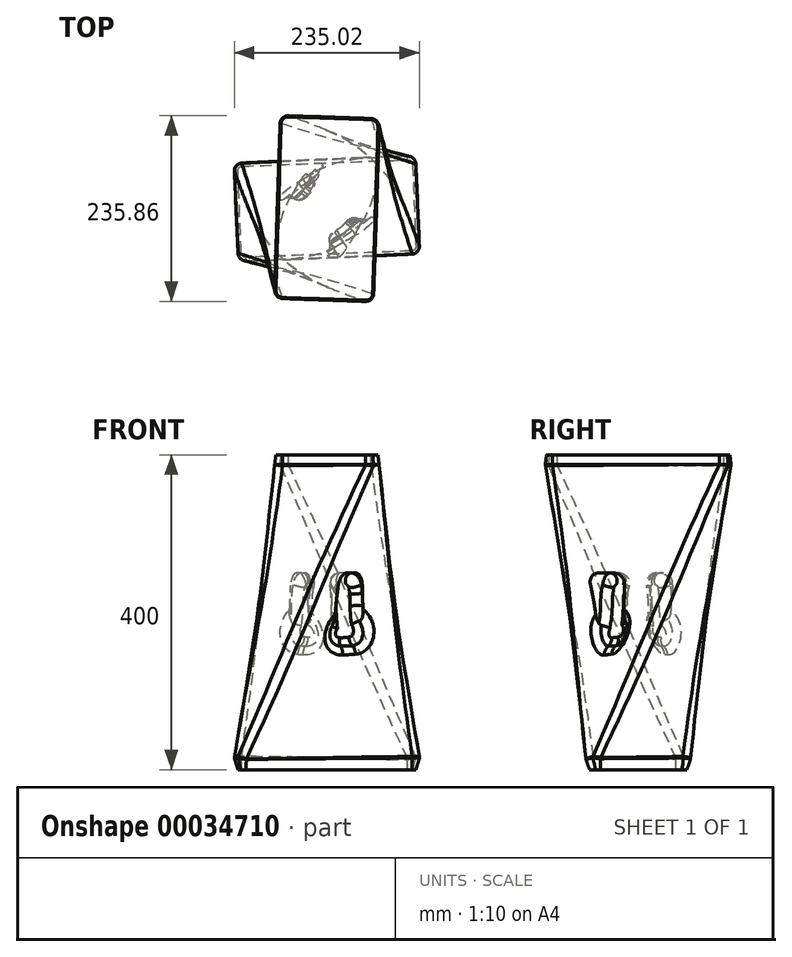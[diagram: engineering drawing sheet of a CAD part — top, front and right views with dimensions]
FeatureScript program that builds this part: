
annotation { "Feature Type Name" : "Feature", "Feature Type Description" : "" }
export const myFeature = defineFeature(function(context is Context, id is Id, definition is map)
    precondition{}
    {
        {
            var Q0;
            Q0=qCreatedBy(makeId("Top.planeOp"),FACE);
            var sketch = newSketch(context, id + "F0", { "sketchPlane" : qUnion([Q0])});
            skLineSegment(sketch, "E0.bottom", {"start": v(-120, 65) * mm, "end": v(120, 65) * mm});
            skLineSegment(sketch, "E0.top", {"start": v(-120, -65) * mm, "end": v(120, -65) * mm});
            skLineSegment(sketch, "E0.left", {"start": v(-120, 65) * mm, "end": v(-120, -65) * mm});
            skLineSegment(sketch, "E0.right", {"start": v(120, 65) * mm, "end": v(120, -65) * mm});
            skSolve(sketch);
        }
        {
            var Q0;
            Q0=qCreatedBy(makeId("Top.planeOp"),FACE);
            cPlane(context, id + "F1", {"entities" : qUnion([Q0]), "cplaneType" : CPlaneType.OFFSET, "offset" : 400 * mm, "width" : 150 * mm, "height" : 150 * mm});
        }
        {
            var Q0;
            Q0=qCreatedBy(id+"F1.planeOp",FACE);
            var sketch = newSketch(context, id + "F2", { "sketchPlane" : qUnion([Q0])});
            skLineSegment(sketch, "E1.bottom", {"start": v(-65, 120) * mm, "end": v(65, 120) * mm});
            skLineSegment(sketch, "E1.top", {"start": v(-65, -120) * mm, "end": v(65, -120) * mm});
            skLineSegment(sketch, "E1.left", {"start": v(-65, 120) * mm, "end": v(-65, -120) * mm});
            skLineSegment(sketch, "E1.right", {"start": v(65, 120) * mm, "end": v(65, -120) * mm});
            skSolve(sketch);
        }
        {
            var Q0;
            Q0=makeQuery(id+"F0.imprint","IMPRINT",FACE,{"disambiguationData":[TD([[makeQuery(id+"F0.imprint","IMPRINT",EDGE,{"derivedFrom":sQuery(id+"F0.wireOp",EDGE,"E0.bottom")}),-1.0]])]});
            var Q1;
            Q1=makeQuery(id+"F2.imprint","IMPRINT",FACE,{"disambiguationData":[TD([[makeQuery(id+"F2.imprint","IMPRINT",EDGE,{"derivedFrom":sQuery(id+"F2.wireOp",EDGE,"E1.bottom")}),-1.0]])]});
            var Q2;
            Q2=sQuery(id+"F0.wireOp",VERTEX,"E0.left.end");
            var Q3;
            Q3=sQuery(id+"F2.wireOp",VERTEX,"E1.top.end");
            loft(context, id + "F3", {"sheetProfilesArray" : [{ "sheetProfileEntities" : qUnion([Q0]) }, { "sheetProfileEntities" : qUnion([Q1]) }], "matchConnections" : true, "connections" : [{ "connectionEntities" : qUnion([Q2, Q3]), "connectionEdgeQueries" : qUnion([]), "connectionEdgeParameters" : [] }]});
        }
        {
            var Q0;
            Q0=makeQuery(id+"F3.opLoft","SWEPT_EDGE",EDGE,{"disambiguationData":[OSD([sQuery(id+"F0.wireOp",EDGE,"E0.top"),sQuery(id+"F0.wireOp",EDGE,"E0.left"),sQuery(id+"F2.wireOp",EDGE,"E1.top"),sQuery(id+"F2.wireOp",EDGE,"E1.right")])]});
            var Q1;
            Q1=makeQuery(id+"F3.opLoft","SWEPT_EDGE",EDGE,{"disambiguationData":[OSD([sQuery(id+"F0.wireOp",EDGE,"E0.bottom"),sQuery(id+"F0.wireOp",EDGE,"E0.left"),sQuery(id+"F2.wireOp",EDGE,"E1.top"),sQuery(id+"F2.wireOp",EDGE,"E1.left")])]});
            var Q2;
            Q2=makeQuery(id+"F3.opLoft","SWEPT_EDGE",EDGE,{"disambiguationData":[OSD([sQuery(id+"F0.wireOp",EDGE,"E0.bottom"),sQuery(id+"F0.wireOp",EDGE,"E0.right"),sQuery(id+"F2.wireOp",EDGE,"E1.bottom"),sQuery(id+"F2.wireOp",EDGE,"E1.left")])]});
            var Q3;
            Q3=makeQuery(id+"F3.opLoft","SWEPT_EDGE",EDGE,{"disambiguationData":[OSD([sQuery(id+"F0.wireOp",EDGE,"E0.top"),sQuery(id+"F0.wireOp",EDGE,"E0.right"),sQuery(id+"F2.wireOp",EDGE,"E1.bottom"),sQuery(id+"F2.wireOp",EDGE,"E1.right")])]});
            fillet(context, id + "F4", {"entities" : qUnion([Q0, Q1, Q2, Q3]), "radius" : 10 * mm, "tangentPropagation" : true, "allowEdgeOverflow" : false});
        }
        {
            var Q0;
            Q0=qCreatedBy(makeId("Front.planeOp"),FACE);
            cPlane(context, id + "F5", {"entities" : qUnion([Q0]), "cplaneType" : CPlaneType.OFFSET, "offset" : 150 * mm, "width" : 150 * mm, "height" : 150 * mm});
        }
        {
            var Q0;
            Q0=qCreatedBy(id+"F5.planeOp",FACE);
            var sketch = newSketch(context, id + "F6", { "sketchPlane" : qUnion([Q0])});
            skLineSegment(sketch, "E2.bottom", {"start": v(-30, 250) * mm, "end": v(30, 250) * mm});
            skLineSegment(sketch, "E2.top", {"start": v(-30, 160) * mm, "end": v(30, 160) * mm});
            skLineSegment(sketch, "E2.left", {"start": v(-30, 250) * mm, "end": v(-30, 160) * mm});
            skLineSegment(sketch, "E2.right", {"start": v(30, 250) * mm, "end": v(30, 160) * mm});
            skSolve(sketch);
        }
        {
            var Q0;
            Q0=qCreatedBy(makeId("Top.planeOp"),FACE);
            cPlane(context, id + "F7", {"entities" : qUnion([Q0]), "cplaneType" : CPlaneType.OFFSET, "offset" : 200 * mm, "width" : 150 * mm, "height" : 150 * mm});
        }
        {
            var Q0;
            Q0=qCreatedBy(id+"F7.planeOp",FACE);
            var sketch = newSketch(context, id + "F8", { "sketchPlane" : qUnion([Q0])});
            skFitSpline(sketch, "E3", {"points": [v(0, -150.22) * mm, v(59.86, -109.69) * mm, v(35.8, -41.64) * mm, v(-107.36, 63.1) * mm], "startDerivative": vector(337.47, 16.1) * mm, "endDerivative": vector(-533.05, 116.89) * mm});
            skSolve(sketch);
        }
        {
            var Q0;
            Q0=makeQuery(id+"F6.imprint","IMPRINT",FACE,{"disambiguationData":[TD([[makeQuery(id+"F6.imprint","IMPRINT",EDGE,{"derivedFrom":sQuery(id+"F6.wireOp",EDGE,"E2.bottom")}),-1.0]])]});
            var Q1;
            Q1=sQuery(id+"F8.wireOp",EDGE,"E3");
            sweep(context, id + "F9", {"operationType" : NewBodyOperationType.REMOVE, "profiles" : qUnion([Q0]), "path" : qUnion([Q1]), "keepProfileOrientation" : true});
        }
        {
            var Q0;
            Q0=makeQuery(id+"F9.boolean.opBoolean","COPY",EDGE,{"derivedFrom":makeQuery(id+"F9.opSweep","SWEPT_EDGE",EDGE,{"disambiguationData":[OSD([sQuery(id+"F6.wireOp",EDGE,"E2.bottom"),sQuery(id+"F6.wireOp",EDGE,"E2.left"),sQuery(id+"F8.wireOp",EDGE,"E3")])]})});
            var Q1;
            Q1=makeQuery(id+"F9.boolean.opBoolean","COPY",EDGE,{"derivedFrom":makeQuery(id+"F9.opSweep","SWEPT_EDGE",EDGE,{"disambiguationData":[OSD([sQuery(id+"F6.wireOp",EDGE,"E2.top"),sQuery(id+"F6.wireOp",EDGE,"E2.right"),sQuery(id+"F8.wireOp",EDGE,"E3")])]})});
            var Q2;
            Q2=makeQuery(id+"F9.boolean.opBoolean","COPY",EDGE,{"derivedFrom":makeQuery(id+"F9.opSweep","SWEPT_EDGE",EDGE,{"disambiguationData":[OSD([sQuery(id+"F6.wireOp",EDGE,"E2.top"),sQuery(id+"F6.wireOp",EDGE,"E2.left"),sQuery(id+"F8.wireOp",EDGE,"E3")])]})});
            var Q3;
            Q3=makeQuery(id+"F9.boolean.opBoolean","COPY",EDGE,{"derivedFrom":makeQuery(id+"F9.opSweep","SWEPT_EDGE",EDGE,{"disambiguationData":[OSD([sQuery(id+"F6.wireOp",EDGE,"E2.bottom"),sQuery(id+"F6.wireOp",EDGE,"E2.right"),sQuery(id+"F8.wireOp",EDGE,"E3")])]})});
            var Q4;
            Q4=makeQuery(id+"F9.boolean.opBoolean","INTERSECT",EDGE,{"derivedFrom":[makeQuery(id+"F3.opLoft","SWEPT_FACE",FACE,{"disambiguationData":[OSD([sQuery(id+"F0.wireOp",EDGE,"E0.top"),sQuery(id+"F0.wireOp",EDGE,"E0.left"),sQuery(id+"F0.wireOp",EDGE,"E0.right"),sQuery(id+"F2.wireOp",EDGE,"E1.bottom"),sQuery(id+"F2.wireOp",EDGE,"E1.top"),sQuery(id+"F2.wireOp",EDGE,"E1.right")])]}),makeQuery(id+"F9.opSweep","SWEPT_FACE",FACE,{"disambiguationData":[OSD([sQuery(id+"F6.wireOp",EDGE,"E2.top"),sQuery(id+"F8.wireOp",EDGE,"E3")])]})]});
            var Q5;
            Q5=makeQuery(id+"F9.boolean.opBoolean","INTERSECT",EDGE,{"derivedFrom":[makeQuery(id+"F3.opLoft","SWEPT_FACE",FACE,{"disambiguationData":[OSD([sQuery(id+"F0.wireOp",EDGE,"E0.bottom"),sQuery(id+"F0.wireOp",EDGE,"E0.left"),sQuery(id+"F0.wireOp",EDGE,"E0.right"),sQuery(id+"F2.wireOp",EDGE,"E1.bottom"),sQuery(id+"F2.wireOp",EDGE,"E1.top"),sQuery(id+"F2.wireOp",EDGE,"E1.left")])]}),makeQuery(id+"F9.opSweep","SWEPT_FACE",FACE,{"disambiguationData":[OSD([sQuery(id+"F6.wireOp",EDGE,"E2.top"),sQuery(id+"F8.wireOp",EDGE,"E3")])]})]});
            fillet(context, id + "F10", {"entities" : qUnion([Q0, Q1, Q2, Q3, Q4, Q5]), "radius" : 15 * mm, "tangentPropagation" : true, "allowEdgeOverflow" : false});
        }
        {
            var Q0;
            Q0=qCreatedBy(makeId("Front.planeOp"),FACE);
            var sketch = newSketch(context, id + "F11", { "sketchPlane" : qUnion([Q0])});
            skFitSpline(sketch, "E4", {"points": [v(0, 259.06) * mm, v(16.44, 250.09) * mm, v(31.7, 233.1) * mm, v(35.53, 197.68) * mm, v(38.17, 168.44) * mm, v(0, 135.83) * mm], "startDerivative": vector(173.2, -65.47) * mm, "endDerivative": vector(-290.13, -212.48) * mm});
            skLineSegment(sketch, "E5", {"start": v(0, 259.06) * mm, "end": v(0, 135.83) * mm});
            skSolve(sketch);
        }
        {
            var Q0;
            Q0=makeQuery(id+"F11.imprint","IMPRINT",FACE,{"disambiguationData":[TD([[makeQuery(id+"F11.imprint","IMPRINT",EDGE,{"derivedFrom":sQuery(id+"F11.wireOp",EDGE,"E4")}),-1.0]])]});
            var Q1;
            Q1=sQuery(id+"F11.wireOp",EDGE,"E5");
            revolve(context, id + "F12", {"operationType" : NewBodyOperationType.ADD, "entities" : qUnion([Q0]), "axis" : qUnion([Q1]), "revolveType" : RevolveType.FULL});
        }
        {
            var Q0;
            Q0=makeQuery(id+"F12.boolean.opBoolean","INTERSECT",EDGE,{"disambiguationData":[OD(1.0)],"derivedFrom":[makeQuery(id+"F9.boolean.opBoolean","COPY",FACE,{"derivedFrom":makeQuery(id+"F9.opSweep","SWEPT_FACE",FACE,{"disambiguationData":[OSD([sQuery(id+"F6.wireOp",EDGE,"E2.bottom"),sQuery(id+"F8.wireOp",EDGE,"E3")])]})}),makeQuery(id+"F12.opRevolve","SWEPT_FACE",FACE,{"disambiguationData":[OSD([sQuery(id+"F11.wireOp",EDGE,"E4")])]})]});
            var Q1;
            Q1=makeQuery(id+"F12.boolean.opBoolean","INTERSECT",EDGE,{"disambiguationData":[OD(0.0)],"derivedFrom":[makeQuery(id+"F10.opFillet","BLEND_FACE",FACE,{"disambiguationData":[OSD([sQuery(id+"F6.wireOp",EDGE,"E2.bottom"),sQuery(id+"F6.wireOp",EDGE,"E2.left"),sQuery(id+"F8.wireOp",EDGE,"E3")])]}),makeQuery(id+"F12.opRevolve","SWEPT_FACE",FACE,{"disambiguationData":[OSD([sQuery(id+"F11.wireOp",EDGE,"E4")])]})]});
            fillet(context, id + "F13", {"entities" : qUnion([Q0, Q1]), "radius" : 10 * mm, "tangentPropagation" : true, "allowEdgeOverflow" : false});
        }
        {
            var Q0;
            Q0=makeQuery(id+"F3.opLoft","MID_CAP_EDGE",EDGE,{"disambiguationData":[OSD([sQuery(id+"F0.wireOp",EDGE,"E0.bottom"),sQuery(id+"F0.wireOp",EDGE,"E0.top"),sQuery(id+"F0.wireOp",EDGE,"E0.right")])],"capPos":0.0});
            chamfer(context, id + "F14", {"entities" : qUnion([Q0]), "chamferType" : ChamferType.TWO_OFFSETS, "width1" : 15 * mm, "oppositeDirection" : false, "width2" : 7 * mm, "tangentPropagation" : true});
        }
        {
            var Q0;
            Q0=makeQuery(id+"F3.opLoft","MID_CAP_EDGE",EDGE,{"disambiguationData":[OSD([sQuery(id+"F2.wireOp",EDGE,"E1.bottom"),sQuery(id+"F2.wireOp",EDGE,"E1.top"),sQuery(id+"F2.wireOp",EDGE,"E1.right")])],"capPos":1.0});
            chamfer(context, id + "F15", {"entities" : qUnion([Q0]), "chamferType" : ChamferType.TWO_OFFSETS, "width1" : 7 * mm, "oppositeDirection" : false, "width2" : 14 * mm, "tangentPropagation" : true});
        }
        {
            var Q0;
            {var subQ0=sQuery(id+"F0.wireOp",EDGE,"E0.right");var subQ1=sQuery(id+"F0.wireOp",EDGE,"E0.top");var subQ2=sQuery(id+"F0.wireOp",EDGE,"E0.bottom");Q0=makeQuery(id+"F14.opChamfer","BLEND_EDGE",EDGE,{"blendedFrom":[makeQuery(id+"F3.opLoft","MID_CAP_EDGE",EDGE,{"disambiguationData":[OSD([subQ2,subQ1,subQ0])],"capPos":0.0}),makeQuery(id+"F3.opLoft","SWEPT_FACE",FACE,{"disambiguationData":[OSD([subQ2,subQ1,subQ0,sQuery(id+"F2.wireOp",EDGE,"E1.bottom"),sQuery(id+"F2.wireOp",EDGE,"E1.left"),sQuery(id+"F2.wireOp",EDGE,"E1.right")])]})],"blendedInto":[makeQuery(id+"F3.opLoft","SWEPT_FACE",FACE,{"disambiguationData":[OSD([subQ2,subQ1,subQ0,sQuery(id+"F2.wireOp",EDGE,"E1.bottom"),sQuery(id+"F2.wireOp",EDGE,"E1.left"),sQuery(id+"F2.wireOp",EDGE,"E1.right")])]})]});}
            var Q1;
            {var subQ0=sQuery(id+"F2.wireOp",EDGE,"E1.right");var subQ1=sQuery(id+"F2.wireOp",EDGE,"E1.bottom");var subQ2=sQuery(id+"F0.wireOp",EDGE,"E0.right");var subQ3=sQuery(id+"F0.wireOp",EDGE,"E0.top");Q1=makeQuery(id+"F14.opChamfer","BLEND_EDGE",EDGE,{"blendedFrom":[makeQuery(id+"F4.opFillet","BLEND_EDGE",EDGE,{"blendedFrom":[makeQuery(id+"F3.opLoft","SWEPT_EDGE",EDGE,{"disambiguationData":[OSD([subQ3,subQ2,subQ1,subQ0])]}),makeQuery(id+"F3.opLoft","CAP_FACE",FACE,{"disambiguationData":[OSD([makeQuery(id+"F0.imprint","IMPRINT",FACE,{"disambiguationData":[TD([[makeQuery(id+"F0.imprint","IMPRINT",EDGE,{"derivedFrom":sQuery(id+"F0.wireOp",EDGE,"E0.bottom")}),-1.0]])]})])],"isStart":true})],"blendedInto":[makeQuery(id+"F3.opLoft","CAP_FACE",FACE,{"disambiguationData":[OSD([makeQuery(id+"F0.imprint","IMPRINT",FACE,{"disambiguationData":[TD([[makeQuery(id+"F0.imprint","IMPRINT",EDGE,{"derivedFrom":sQuery(id+"F0.wireOp",EDGE,"E0.bottom")}),-1.0]])]})])],"isStart":true})]}),makeQuery(id+"F4.opFillet","BLEND_FACE",FACE,{"disambiguationData":[OSD([subQ3,subQ2,subQ1,subQ0])]})],"blendedInto":[makeQuery(id+"F4.opFillet","BLEND_FACE",FACE,{"disambiguationData":[OSD([subQ3,subQ2,subQ1,subQ0])]})]});}
            var Q2;
            {var subQ0=sQuery(id+"F0.wireOp",EDGE,"E0.right");var subQ1=sQuery(id+"F0.wireOp",EDGE,"E0.left");var subQ2=sQuery(id+"F0.wireOp",EDGE,"E0.top");Q2=makeQuery(id+"F14.opChamfer","BLEND_EDGE",EDGE,{"blendedFrom":[makeQuery(id+"F3.opLoft","MID_CAP_EDGE",EDGE,{"disambiguationData":[OSD([subQ2,subQ1,subQ0])],"capPos":0.0}),makeQuery(id+"F3.opLoft","SWEPT_FACE",FACE,{"disambiguationData":[OSD([subQ2,subQ1,subQ0,sQuery(id+"F2.wireOp",EDGE,"E1.bottom"),sQuery(id+"F2.wireOp",EDGE,"E1.top"),sQuery(id+"F2.wireOp",EDGE,"E1.right")])]})],"blendedInto":[makeQuery(id+"F3.opLoft","SWEPT_FACE",FACE,{"disambiguationData":[OSD([subQ2,subQ1,subQ0,sQuery(id+"F2.wireOp",EDGE,"E1.bottom"),sQuery(id+"F2.wireOp",EDGE,"E1.top"),sQuery(id+"F2.wireOp",EDGE,"E1.right")])]})]});}
            var Q3;
            {var subQ0=sQuery(id+"F2.wireOp",EDGE,"E1.right");var subQ1=sQuery(id+"F2.wireOp",EDGE,"E1.top");var subQ2=sQuery(id+"F0.wireOp",EDGE,"E0.left");var subQ3=sQuery(id+"F0.wireOp",EDGE,"E0.top");Q3=makeQuery(id+"F14.opChamfer","BLEND_EDGE",EDGE,{"blendedFrom":[makeQuery(id+"F4.opFillet","BLEND_EDGE",EDGE,{"blendedFrom":[makeQuery(id+"F3.opLoft","SWEPT_EDGE",EDGE,{"disambiguationData":[OSD([subQ3,subQ2,subQ1,subQ0])]}),makeQuery(id+"F3.opLoft","CAP_FACE",FACE,{"disambiguationData":[OSD([makeQuery(id+"F0.imprint","IMPRINT",FACE,{"disambiguationData":[TD([[makeQuery(id+"F0.imprint","IMPRINT",EDGE,{"derivedFrom":sQuery(id+"F0.wireOp",EDGE,"E0.bottom")}),-1.0]])]})])],"isStart":true})],"blendedInto":[makeQuery(id+"F3.opLoft","CAP_FACE",FACE,{"disambiguationData":[OSD([makeQuery(id+"F0.imprint","IMPRINT",FACE,{"disambiguationData":[TD([[makeQuery(id+"F0.imprint","IMPRINT",EDGE,{"derivedFrom":sQuery(id+"F0.wireOp",EDGE,"E0.bottom")}),-1.0]])]})])],"isStart":true})]}),makeQuery(id+"F4.opFillet","BLEND_FACE",FACE,{"disambiguationData":[OSD([subQ3,subQ2,subQ1,subQ0])]})],"blendedInto":[makeQuery(id+"F4.opFillet","BLEND_FACE",FACE,{"disambiguationData":[OSD([subQ3,subQ2,subQ1,subQ0])]})]});}
            var Q4;
            {var subQ0=sQuery(id+"F0.wireOp",EDGE,"E0.left");var subQ1=sQuery(id+"F0.wireOp",EDGE,"E0.top");var subQ2=sQuery(id+"F0.wireOp",EDGE,"E0.bottom");Q4=makeQuery(id+"F14.opChamfer","BLEND_EDGE",EDGE,{"blendedFrom":[makeQuery(id+"F3.opLoft","MID_CAP_EDGE",EDGE,{"disambiguationData":[OSD([subQ2,subQ1,subQ0])],"capPos":0.0}),makeQuery(id+"F3.opLoft","SWEPT_FACE",FACE,{"disambiguationData":[OSD([subQ2,subQ1,subQ0,sQuery(id+"F2.wireOp",EDGE,"E1.top"),sQuery(id+"F2.wireOp",EDGE,"E1.left"),sQuery(id+"F2.wireOp",EDGE,"E1.right")])]})],"blendedInto":[makeQuery(id+"F3.opLoft","SWEPT_FACE",FACE,{"disambiguationData":[OSD([subQ2,subQ1,subQ0,sQuery(id+"F2.wireOp",EDGE,"E1.top"),sQuery(id+"F2.wireOp",EDGE,"E1.left"),sQuery(id+"F2.wireOp",EDGE,"E1.right")])]})]});}
            var Q5;
            {var subQ0=sQuery(id+"F2.wireOp",EDGE,"E1.left");var subQ1=sQuery(id+"F2.wireOp",EDGE,"E1.bottom");var subQ2=sQuery(id+"F0.wireOp",EDGE,"E0.right");var subQ3=sQuery(id+"F0.wireOp",EDGE,"E0.bottom");Q5=makeQuery(id+"F14.opChamfer","BLEND_EDGE",EDGE,{"blendedFrom":[makeQuery(id+"F4.opFillet","BLEND_EDGE",EDGE,{"blendedFrom":[makeQuery(id+"F3.opLoft","SWEPT_EDGE",EDGE,{"disambiguationData":[OSD([subQ3,subQ2,subQ1,subQ0])]}),makeQuery(id+"F3.opLoft","CAP_FACE",FACE,{"disambiguationData":[OSD([makeQuery(id+"F0.imprint","IMPRINT",FACE,{"disambiguationData":[TD([[makeQuery(id+"F0.imprint","IMPRINT",EDGE,{"derivedFrom":subQ3}),-1.0]])]})])],"isStart":true})],"blendedInto":[makeQuery(id+"F3.opLoft","CAP_FACE",FACE,{"disambiguationData":[OSD([makeQuery(id+"F0.imprint","IMPRINT",FACE,{"disambiguationData":[TD([[makeQuery(id+"F0.imprint","IMPRINT",EDGE,{"derivedFrom":subQ3}),-1.0]])]})])],"isStart":true})]}),makeQuery(id+"F4.opFillet","BLEND_FACE",FACE,{"disambiguationData":[OSD([subQ3,subQ2,subQ1,subQ0])]})],"blendedInto":[makeQuery(id+"F4.opFillet","BLEND_FACE",FACE,{"disambiguationData":[OSD([subQ3,subQ2,subQ1,subQ0])]})]});}
            var Q6;
            {var subQ0=sQuery(id+"F0.wireOp",EDGE,"E0.right");var subQ1=sQuery(id+"F0.wireOp",EDGE,"E0.left");var subQ2=sQuery(id+"F0.wireOp",EDGE,"E0.bottom");Q6=makeQuery(id+"F14.opChamfer","BLEND_EDGE",EDGE,{"blendedFrom":[makeQuery(id+"F3.opLoft","MID_CAP_EDGE",EDGE,{"disambiguationData":[OSD([subQ2,subQ1,subQ0])],"capPos":0.0}),makeQuery(id+"F3.opLoft","SWEPT_FACE",FACE,{"disambiguationData":[OSD([subQ2,subQ1,subQ0,sQuery(id+"F2.wireOp",EDGE,"E1.bottom"),sQuery(id+"F2.wireOp",EDGE,"E1.top"),sQuery(id+"F2.wireOp",EDGE,"E1.left")])]})],"blendedInto":[makeQuery(id+"F3.opLoft","SWEPT_FACE",FACE,{"disambiguationData":[OSD([subQ2,subQ1,subQ0,sQuery(id+"F2.wireOp",EDGE,"E1.bottom"),sQuery(id+"F2.wireOp",EDGE,"E1.top"),sQuery(id+"F2.wireOp",EDGE,"E1.left")])]})]});}
            var Q7;
            {var subQ0=sQuery(id+"F2.wireOp",EDGE,"E1.left");var subQ1=sQuery(id+"F2.wireOp",EDGE,"E1.top");var subQ2=sQuery(id+"F0.wireOp",EDGE,"E0.left");var subQ3=sQuery(id+"F0.wireOp",EDGE,"E0.bottom");Q7=makeQuery(id+"F14.opChamfer","BLEND_EDGE",EDGE,{"blendedFrom":[makeQuery(id+"F4.opFillet","BLEND_EDGE",EDGE,{"blendedFrom":[makeQuery(id+"F3.opLoft","SWEPT_EDGE",EDGE,{"disambiguationData":[OSD([subQ3,subQ2,subQ1,subQ0])]}),makeQuery(id+"F3.opLoft","CAP_FACE",FACE,{"disambiguationData":[OSD([makeQuery(id+"F0.imprint","IMPRINT",FACE,{"disambiguationData":[TD([[makeQuery(id+"F0.imprint","IMPRINT",EDGE,{"derivedFrom":subQ3}),-1.0]])]})])],"isStart":true})],"blendedInto":[makeQuery(id+"F3.opLoft","CAP_FACE",FACE,{"disambiguationData":[OSD([makeQuery(id+"F0.imprint","IMPRINT",FACE,{"disambiguationData":[TD([[makeQuery(id+"F0.imprint","IMPRINT",EDGE,{"derivedFrom":subQ3}),-1.0]])]})])],"isStart":true})]}),makeQuery(id+"F4.opFillet","BLEND_FACE",FACE,{"disambiguationData":[OSD([subQ3,subQ2,subQ1,subQ0])]})],"blendedInto":[makeQuery(id+"F4.opFillet","BLEND_FACE",FACE,{"disambiguationData":[OSD([subQ3,subQ2,subQ1,subQ0])]})]});}
            var Q8;
            {var subQ0=sQuery(id+"F2.wireOp",EDGE,"E1.left");var subQ1=sQuery(id+"F2.wireOp",EDGE,"E1.top");var subQ2=sQuery(id+"F0.wireOp",EDGE,"E0.left");var subQ3=sQuery(id+"F0.wireOp",EDGE,"E0.bottom");Q8=makeQuery(id+"F15.opChamfer","BLEND_EDGE",EDGE,{"blendedFrom":[makeQuery(id+"F4.opFillet","BLEND_EDGE",EDGE,{"blendedFrom":[makeQuery(id+"F3.opLoft","SWEPT_EDGE",EDGE,{"disambiguationData":[OSD([subQ3,subQ2,subQ1,subQ0])]}),makeQuery(id+"F3.opLoft","CAP_FACE",FACE,{"disambiguationData":[OSD([makeQuery(id+"F2.imprint","IMPRINT",FACE,{"disambiguationData":[TD([[makeQuery(id+"F2.imprint","IMPRINT",EDGE,{"derivedFrom":sQuery(id+"F2.wireOp",EDGE,"E1.bottom")}),-1.0]])]})])],"isStart":true})],"blendedInto":[makeQuery(id+"F3.opLoft","CAP_FACE",FACE,{"disambiguationData":[OSD([makeQuery(id+"F2.imprint","IMPRINT",FACE,{"disambiguationData":[TD([[makeQuery(id+"F2.imprint","IMPRINT",EDGE,{"derivedFrom":sQuery(id+"F2.wireOp",EDGE,"E1.bottom")}),-1.0]])]})])],"isStart":true})]}),makeQuery(id+"F4.opFillet","BLEND_FACE",FACE,{"disambiguationData":[OSD([subQ3,subQ2,subQ1,subQ0])]})],"blendedInto":[makeQuery(id+"F4.opFillet","BLEND_FACE",FACE,{"disambiguationData":[OSD([subQ3,subQ2,subQ1,subQ0])]})]});}
            var Q9;
            {var subQ0=sQuery(id+"F2.wireOp",EDGE,"E1.left");var subQ1=sQuery(id+"F2.wireOp",EDGE,"E1.top");var subQ2=sQuery(id+"F2.wireOp",EDGE,"E1.bottom");Q9=makeQuery(id+"F15.opChamfer","BLEND_EDGE",EDGE,{"blendedFrom":[makeQuery(id+"F3.opLoft","MID_CAP_EDGE",EDGE,{"disambiguationData":[OSD([subQ2,subQ1,subQ0])],"capPos":1.0}),makeQuery(id+"F3.opLoft","SWEPT_FACE",FACE,{"disambiguationData":[OSD([sQuery(id+"F0.wireOp",EDGE,"E0.bottom"),sQuery(id+"F0.wireOp",EDGE,"E0.left"),sQuery(id+"F0.wireOp",EDGE,"E0.right"),subQ2,subQ1,subQ0])]})],"blendedInto":[makeQuery(id+"F3.opLoft","SWEPT_FACE",FACE,{"disambiguationData":[OSD([sQuery(id+"F0.wireOp",EDGE,"E0.bottom"),sQuery(id+"F0.wireOp",EDGE,"E0.left"),sQuery(id+"F0.wireOp",EDGE,"E0.right"),subQ2,subQ1,subQ0])]})]});}
            var Q10;
            {var subQ0=sQuery(id+"F2.wireOp",EDGE,"E1.left");var subQ1=sQuery(id+"F2.wireOp",EDGE,"E1.bottom");var subQ2=sQuery(id+"F0.wireOp",EDGE,"E0.right");var subQ3=sQuery(id+"F0.wireOp",EDGE,"E0.bottom");Q10=makeQuery(id+"F15.opChamfer","BLEND_EDGE",EDGE,{"blendedFrom":[makeQuery(id+"F4.opFillet","BLEND_EDGE",EDGE,{"blendedFrom":[makeQuery(id+"F3.opLoft","SWEPT_EDGE",EDGE,{"disambiguationData":[OSD([subQ3,subQ2,subQ1,subQ0])]}),makeQuery(id+"F3.opLoft","CAP_FACE",FACE,{"disambiguationData":[OSD([makeQuery(id+"F2.imprint","IMPRINT",FACE,{"disambiguationData":[TD([[makeQuery(id+"F2.imprint","IMPRINT",EDGE,{"derivedFrom":subQ1}),-1.0]])]})])],"isStart":true})],"blendedInto":[makeQuery(id+"F3.opLoft","CAP_FACE",FACE,{"disambiguationData":[OSD([makeQuery(id+"F2.imprint","IMPRINT",FACE,{"disambiguationData":[TD([[makeQuery(id+"F2.imprint","IMPRINT",EDGE,{"derivedFrom":subQ1}),-1.0]])]})])],"isStart":true})]}),makeQuery(id+"F4.opFillet","BLEND_FACE",FACE,{"disambiguationData":[OSD([subQ3,subQ2,subQ1,subQ0])]})],"blendedInto":[makeQuery(id+"F4.opFillet","BLEND_FACE",FACE,{"disambiguationData":[OSD([subQ3,subQ2,subQ1,subQ0])]})]});}
            var Q11;
            {var subQ0=sQuery(id+"F2.wireOp",EDGE,"E1.right");var subQ1=sQuery(id+"F2.wireOp",EDGE,"E1.left");var subQ2=sQuery(id+"F2.wireOp",EDGE,"E1.bottom");Q11=makeQuery(id+"F15.opChamfer","BLEND_EDGE",EDGE,{"blendedFrom":[makeQuery(id+"F3.opLoft","MID_CAP_EDGE",EDGE,{"disambiguationData":[OSD([subQ2,subQ1,subQ0])],"capPos":1.0}),makeQuery(id+"F3.opLoft","SWEPT_FACE",FACE,{"disambiguationData":[OSD([sQuery(id+"F0.wireOp",EDGE,"E0.bottom"),sQuery(id+"F0.wireOp",EDGE,"E0.top"),sQuery(id+"F0.wireOp",EDGE,"E0.right"),subQ2,subQ1,subQ0])]})],"blendedInto":[makeQuery(id+"F3.opLoft","SWEPT_FACE",FACE,{"disambiguationData":[OSD([sQuery(id+"F0.wireOp",EDGE,"E0.bottom"),sQuery(id+"F0.wireOp",EDGE,"E0.top"),sQuery(id+"F0.wireOp",EDGE,"E0.right"),subQ2,subQ1,subQ0])]})]});}
            var Q12;
            {var subQ0=sQuery(id+"F2.wireOp",EDGE,"E1.right");var subQ1=sQuery(id+"F2.wireOp",EDGE,"E1.bottom");var subQ2=sQuery(id+"F0.wireOp",EDGE,"E0.right");var subQ3=sQuery(id+"F0.wireOp",EDGE,"E0.top");Q12=makeQuery(id+"F15.opChamfer","BLEND_EDGE",EDGE,{"blendedFrom":[makeQuery(id+"F4.opFillet","BLEND_EDGE",EDGE,{"blendedFrom":[makeQuery(id+"F3.opLoft","SWEPT_EDGE",EDGE,{"disambiguationData":[OSD([subQ3,subQ2,subQ1,subQ0])]}),makeQuery(id+"F3.opLoft","CAP_FACE",FACE,{"disambiguationData":[OSD([makeQuery(id+"F2.imprint","IMPRINT",FACE,{"disambiguationData":[TD([[makeQuery(id+"F2.imprint","IMPRINT",EDGE,{"derivedFrom":subQ1}),-1.0]])]})])],"isStart":true})],"blendedInto":[makeQuery(id+"F3.opLoft","CAP_FACE",FACE,{"disambiguationData":[OSD([makeQuery(id+"F2.imprint","IMPRINT",FACE,{"disambiguationData":[TD([[makeQuery(id+"F2.imprint","IMPRINT",EDGE,{"derivedFrom":subQ1}),-1.0]])]})])],"isStart":true})]}),makeQuery(id+"F4.opFillet","BLEND_FACE",FACE,{"disambiguationData":[OSD([subQ3,subQ2,subQ1,subQ0])]})],"blendedInto":[makeQuery(id+"F4.opFillet","BLEND_FACE",FACE,{"disambiguationData":[OSD([subQ3,subQ2,subQ1,subQ0])]})]});}
            var Q13;
            {var subQ0=sQuery(id+"F2.wireOp",EDGE,"E1.right");var subQ1=sQuery(id+"F2.wireOp",EDGE,"E1.top");var subQ2=sQuery(id+"F2.wireOp",EDGE,"E1.bottom");Q13=makeQuery(id+"F15.opChamfer","BLEND_EDGE",EDGE,{"blendedFrom":[makeQuery(id+"F3.opLoft","MID_CAP_EDGE",EDGE,{"disambiguationData":[OSD([subQ2,subQ1,subQ0])],"capPos":1.0}),makeQuery(id+"F3.opLoft","SWEPT_FACE",FACE,{"disambiguationData":[OSD([sQuery(id+"F0.wireOp",EDGE,"E0.top"),sQuery(id+"F0.wireOp",EDGE,"E0.left"),sQuery(id+"F0.wireOp",EDGE,"E0.right"),subQ2,subQ1,subQ0])]})],"blendedInto":[makeQuery(id+"F3.opLoft","SWEPT_FACE",FACE,{"disambiguationData":[OSD([sQuery(id+"F0.wireOp",EDGE,"E0.top"),sQuery(id+"F0.wireOp",EDGE,"E0.left"),sQuery(id+"F0.wireOp",EDGE,"E0.right"),subQ2,subQ1,subQ0])]})]});}
            var Q14;
            {var subQ0=sQuery(id+"F2.wireOp",EDGE,"E1.right");var subQ1=sQuery(id+"F2.wireOp",EDGE,"E1.top");var subQ2=sQuery(id+"F0.wireOp",EDGE,"E0.left");var subQ3=sQuery(id+"F0.wireOp",EDGE,"E0.top");Q14=makeQuery(id+"F15.opChamfer","BLEND_EDGE",EDGE,{"blendedFrom":[makeQuery(id+"F4.opFillet","BLEND_EDGE",EDGE,{"blendedFrom":[makeQuery(id+"F3.opLoft","SWEPT_EDGE",EDGE,{"disambiguationData":[OSD([subQ3,subQ2,subQ1,subQ0])]}),makeQuery(id+"F3.opLoft","CAP_FACE",FACE,{"disambiguationData":[OSD([makeQuery(id+"F2.imprint","IMPRINT",FACE,{"disambiguationData":[TD([[makeQuery(id+"F2.imprint","IMPRINT",EDGE,{"derivedFrom":sQuery(id+"F2.wireOp",EDGE,"E1.bottom")}),-1.0]])]})])],"isStart":true})],"blendedInto":[makeQuery(id+"F3.opLoft","CAP_FACE",FACE,{"disambiguationData":[OSD([makeQuery(id+"F2.imprint","IMPRINT",FACE,{"disambiguationData":[TD([[makeQuery(id+"F2.imprint","IMPRINT",EDGE,{"derivedFrom":sQuery(id+"F2.wireOp",EDGE,"E1.bottom")}),-1.0]])]})])],"isStart":true})]}),makeQuery(id+"F4.opFillet","BLEND_FACE",FACE,{"disambiguationData":[OSD([subQ3,subQ2,subQ1,subQ0])]})],"blendedInto":[makeQuery(id+"F4.opFillet","BLEND_FACE",FACE,{"disambiguationData":[OSD([subQ3,subQ2,subQ1,subQ0])]})]});}
            fillet(context, id + "F16", {"entities" : qUnion([Q0, Q1, Q2, Q3, Q4, Q5, Q6, Q7, Q8, Q9, Q10, Q11, Q12, Q13, Q14]), "radius" : 3 * mm, "tangentPropagation" : true, "allowEdgeOverflow" : false});
        }
    });
